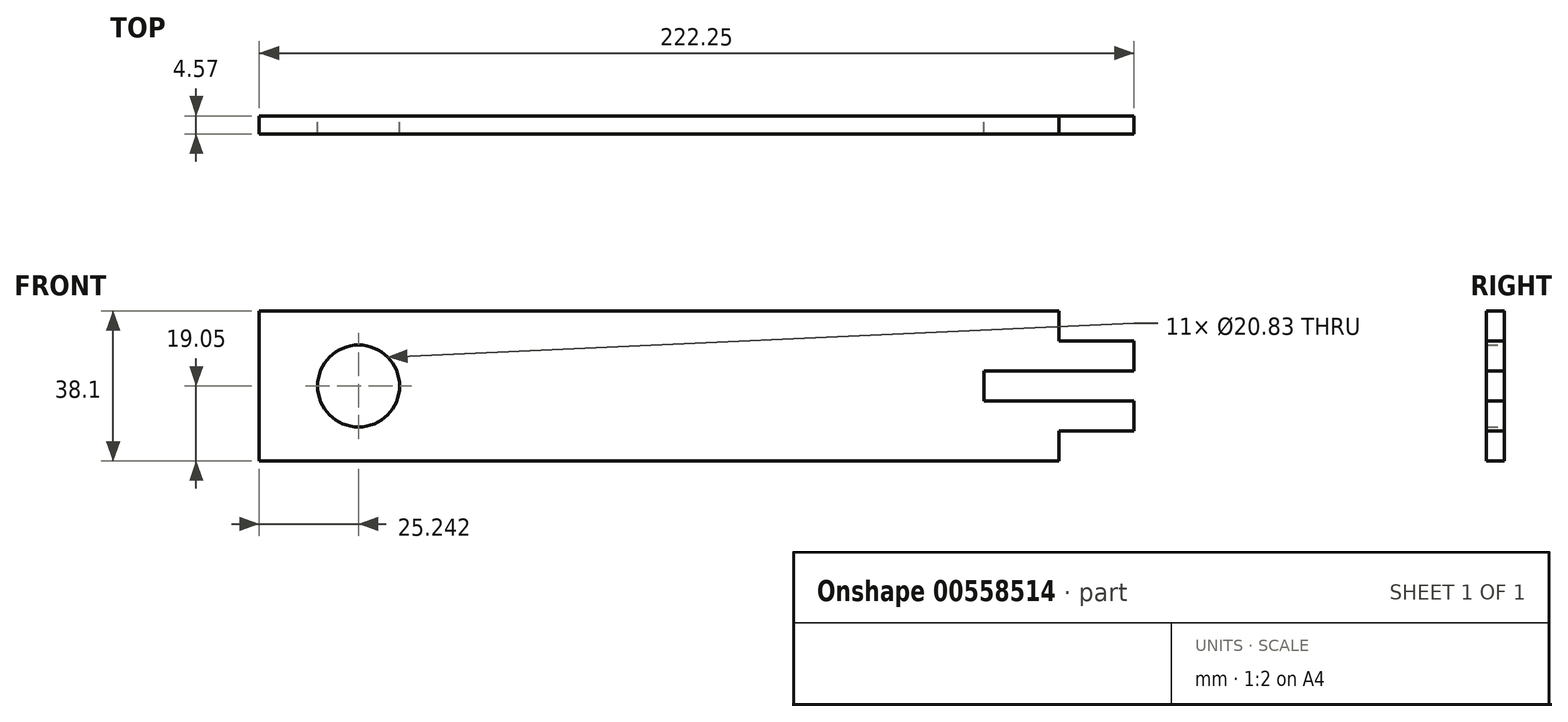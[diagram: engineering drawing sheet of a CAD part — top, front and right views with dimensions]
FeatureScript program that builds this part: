
annotation { "Feature Type Name" : "Feature", "Feature Type Description" : "" }
export const myFeature = defineFeature(function(context is Context, id is Id, definition is map)
    precondition{}
    {
        {
            var Q0;
            Q0=qCreatedBy(makeId("Front.planeOp"),FACE);
            var sketch = newSketch(context, id + "F0", { "sketchPlane" : qUnion([Q0])});
            skLineSegment(sketch, "E0.bottom", {"start": v(101.6, -19.05) * mm, "end": v(-101.6, -19.05) * mm});
            skLineSegment(sketch, "E0.top", {"start": v(101.6, 19.05) * mm, "end": v(-101.6, 19.05) * mm});
            skLineSegment(sketch, "E0.left", {"start": v(101.6, -19.05) * mm, "end": v(101.6, 19.05) * mm});
            skLineSegment(sketch, "E0.right", {"start": v(-101.6, -19.05) * mm, "end": v(-101.6, 19.05) * mm});
            skPoint(sketch, "E0.middle", {"position": v(0, 0) * mm});
            skCircle(sketch, "E1", {"center": v(-76.36, 0) * mm, "radius": 10.41 * mm});
            skLineSegment(sketch, "E2.bottom", {"start": v(101.6, 3.8) * mm, "end": v(82.55, 3.8) * mm});
            skLineSegment(sketch, "E2.top", {"start": v(101.6, -3.8) * mm, "end": v(82.55, -3.8) * mm});
            skLineSegment(sketch, "E2.right", {"start": v(82.55, 3.8) * mm, "end": v(82.55, -3.8) * mm});
            skPoint(sketch, "E2.middle", {"position": v(92.07, 0) * mm});
            skLineSegment(sketch, "E3.bottom", {"start": v(101.6, 3.8) * mm, "end": v(120.65, 3.8) * mm});
            skLineSegment(sketch, "E3.top", {"start": v(101.6, 11.43) * mm, "end": v(120.65, 11.43) * mm});
            skLineSegment(sketch, "E3.left", {"start": v(101.6, 3.8) * mm, "end": v(101.6, 11.43) * mm});
            skLineSegment(sketch, "E3.right", {"start": v(120.65, 3.8) * mm, "end": v(120.65, 11.43) * mm});
            skLineSegment(sketch, "E4.bottom", {"start": v(101.6, -3.8) * mm, "end": v(120.65, -3.8) * mm});
            skLineSegment(sketch, "E4.top", {"start": v(101.6, -11.43) * mm, "end": v(120.65, -11.43) * mm});
            skLineSegment(sketch, "E4.left", {"start": v(101.6, -3.8) * mm, "end": v(101.6, -11.43) * mm});
            skLineSegment(sketch, "E4.right", {"start": v(120.65, -3.8) * mm, "end": v(120.65, -11.43) * mm});
            skSolve(sketch);
        }
        {
            var Q0;
            {var subQ3=sQuery(id+"F0.wireOp",EDGE,"E0.bottom");Q0=makeQuery(id+"F0.imprint","IMPRINT",FACE,{"disambiguationData":[TD([[makeQuery(id+"F0.imprint","IMPRINT",EDGE,{"derivedFrom":subQ3}),-1.0]])]});}
            var Q1;
            Q1=makeQuery(id+"F0.imprint","IMPRINT",FACE,{"disambiguationData":[TD([[makeQuery(id+"F0.imprint","IMPRINT",EDGE,{"derivedFrom":sQuery(id+"F0.wireOp",EDGE,"E3.bottom")}),1.0]])]});
            var Q2;
            Q2=makeQuery(id+"F0.imprint","IMPRINT",FACE,{"disambiguationData":[TD([[makeQuery(id+"F0.imprint","IMPRINT",EDGE,{"derivedFrom":sQuery(id+"F0.wireOp",EDGE,"E4.bottom")}),-1.0]])]});
            extrude(context, id + "F1", {"entities" : qUnion([Q0, Q1, Q2]), "depth" : 4.57 * mm, "offsetDistance" : 25.4 * mm});
        }
    });
